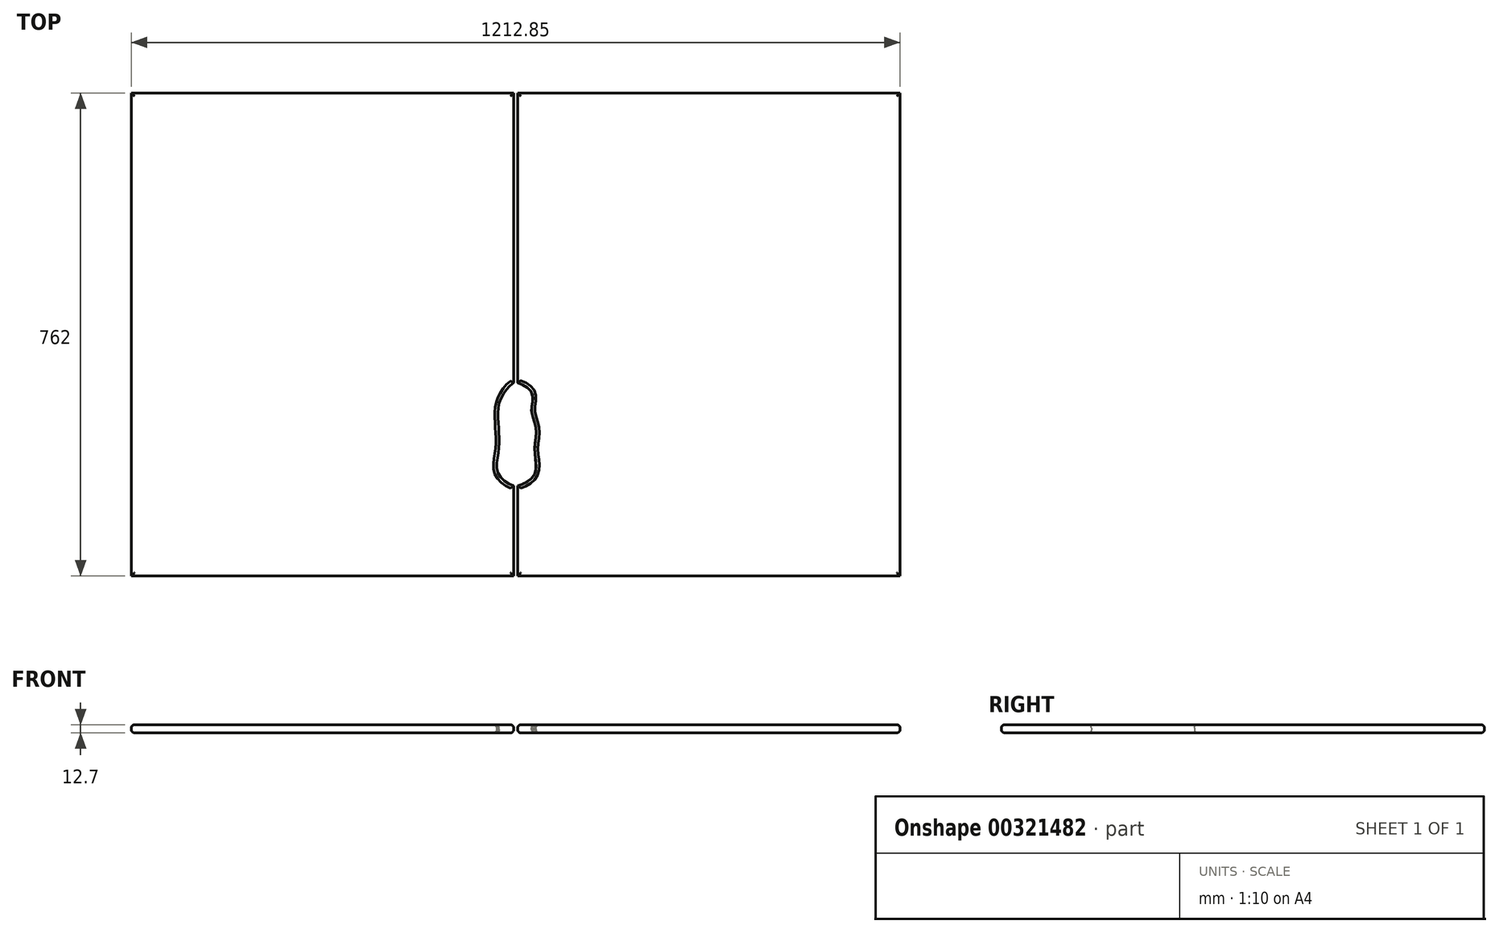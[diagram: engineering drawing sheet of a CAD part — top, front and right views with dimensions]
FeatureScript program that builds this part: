
annotation { "Feature Type Name" : "Feature", "Feature Type Description" : "" }
export const myFeature = defineFeature(function(context is Context, id is Id, definition is map)
    precondition{}
    {
        {
            var Q0;
            Q0=qCreatedBy(makeId("Top.planeOp"),FACE);
            var sketch = newSketch(context, id + "F0", { "sketchPlane" : qUnion([Q0])});
            skLineSegment(sketch, "E0.bottom", {"start": v(-1274.78, 389.18) * mm, "end": v(-671.53, 389.18) * mm});
            skLineSegment(sketch, "E0.top", {"start": v(-1274.78, -372.82) * mm, "end": v(-671.53, -372.82) * mm});
            skLineSegment(sketch, "E0.left", {"start": v(-1274.78, 389.18) * mm, "end": v(-1274.78, -372.82) * mm});
            skLineSegment(sketch, "E0.right", {"start": v(-671.53, 389.18) * mm, "end": v(-671.53, -372.82) * mm});
            skLineSegment(sketch, "E1.bottom", {"start": v(-665.18, 389.18) * mm, "end": v(-61.93, 389.18) * mm});
            skLineSegment(sketch, "E1.top", {"start": v(-665.18, -372.82) * mm, "end": v(-61.93, -372.82) * mm});
            skLineSegment(sketch, "E1.left", {"start": v(-665.18, 389.18) * mm, "end": v(-665.18, -372.82) * mm});
            skLineSegment(sketch, "E1.right", {"start": v(-61.93, 389.18) * mm, "end": v(-61.93, -372.82) * mm});
            skFitSpline(sketch, "E2", {"points": [v(-671.53, -68.2) * mm, v(-692.19, -94.21) * mm, v(-695.44, -138.13) * mm, v(-695.44, -175.54) * mm, v(-695.44, -212.94) * mm, v(-671.53, -230.84) * mm, v(-665.18, -230.84) * mm, v(-639.5, -214.2) * mm, v(-638.27, -174.78) * mm, v(-636.43, -140.28) * mm, v(-643.2, -114.4) * mm, v(-641.35, -95.31) * mm, v(-646.28, -78.68) * mm, v(-665.18, -68.2) * mm, v(-671.53, -68.2) * mm]});
            skSolve(sketch);
        }
        {
            var Q0;
            Q0=makeQuery(id+"F0.imprint","IMPRINT",FACE,{"disambiguationData":[TD([[makeQuery(id+"F0.imprint","IMPRINT",EDGE,{"derivedFrom":sQuery(id+"F0.wireOp",EDGE,"E1.bottom")}),-1.0]])]});
            var Q1;
            Q1=makeQuery(id+"F0.imprint","IMPRINT",FACE,{"disambiguationData":[TD([[makeQuery(id+"F0.imprint","IMPRINT",EDGE,{"derivedFrom":sQuery(id+"F0.wireOp",EDGE,"E0.bottom")}),-1.0]])]});
            extrude(context, id + "F1", {"entities" : qUnion([Q0, Q1]), "depth" : 12.7 * mm});
        }
        {
            var Q0;
            Q0=makeQuery(id+"F1.opExtrude","CAP_FACE",FACE,{"disambiguationData":[OSD([sQuery(id+"F0.wireOp",EDGE,"E0.bottom"),sQuery(id+"F0.wireOp",EDGE,"E0.top"),sQuery(id+"F0.wireOp",EDGE,"E0.left"),sQuery(id+"F0.wireOp",EDGE,"E0.right"),sQuery(id+"F0.wireOp",EDGE,"E2")])],"isStart":false});
            var Q1;
            Q1=makeQuery(id+"F1.opExtrude","CAP_FACE",FACE,{"disambiguationData":[OSD([sQuery(id+"F0.wireOp",EDGE,"E1.bottom"),sQuery(id+"F0.wireOp",EDGE,"E1.top"),sQuery(id+"F0.wireOp",EDGE,"E1.left"),sQuery(id+"F0.wireOp",EDGE,"E1.right"),sQuery(id+"F0.wireOp",EDGE,"E2")])],"isStart":false});
            fillet(context, id + "F2", {"entities" : qUnion([Q0, Q1]), "radius" : 5.08 * mm, "tangentPropagation" : true, "allowEdgeOverflow" : false});
        }
        {
            var Q0;
            Q0=makeQuery(id+"F1.opExtrude","CAP_FACE",FACE,{"disambiguationData":[OSD([sQuery(id+"F0.wireOp",EDGE,"E0.bottom"),sQuery(id+"F0.wireOp",EDGE,"E0.top"),sQuery(id+"F0.wireOp",EDGE,"E0.left"),sQuery(id+"F0.wireOp",EDGE,"E0.right"),sQuery(id+"F0.wireOp",EDGE,"E2")])],"isStart":true});
            var Q1;
            Q1=makeQuery(id+"F1.opExtrude","CAP_FACE",FACE,{"disambiguationData":[OSD([sQuery(id+"F0.wireOp",EDGE,"E1.bottom"),sQuery(id+"F0.wireOp",EDGE,"E1.top"),sQuery(id+"F0.wireOp",EDGE,"E1.left"),sQuery(id+"F0.wireOp",EDGE,"E1.right"),sQuery(id+"F0.wireOp",EDGE,"E2")])],"isStart":true});
            fillet(context, id + "F3", {"entities" : qUnion([Q0, Q1]), "radius" : 5.08 * mm, "tangentPropagation" : true, "allowEdgeOverflow" : false});
        }
    });
